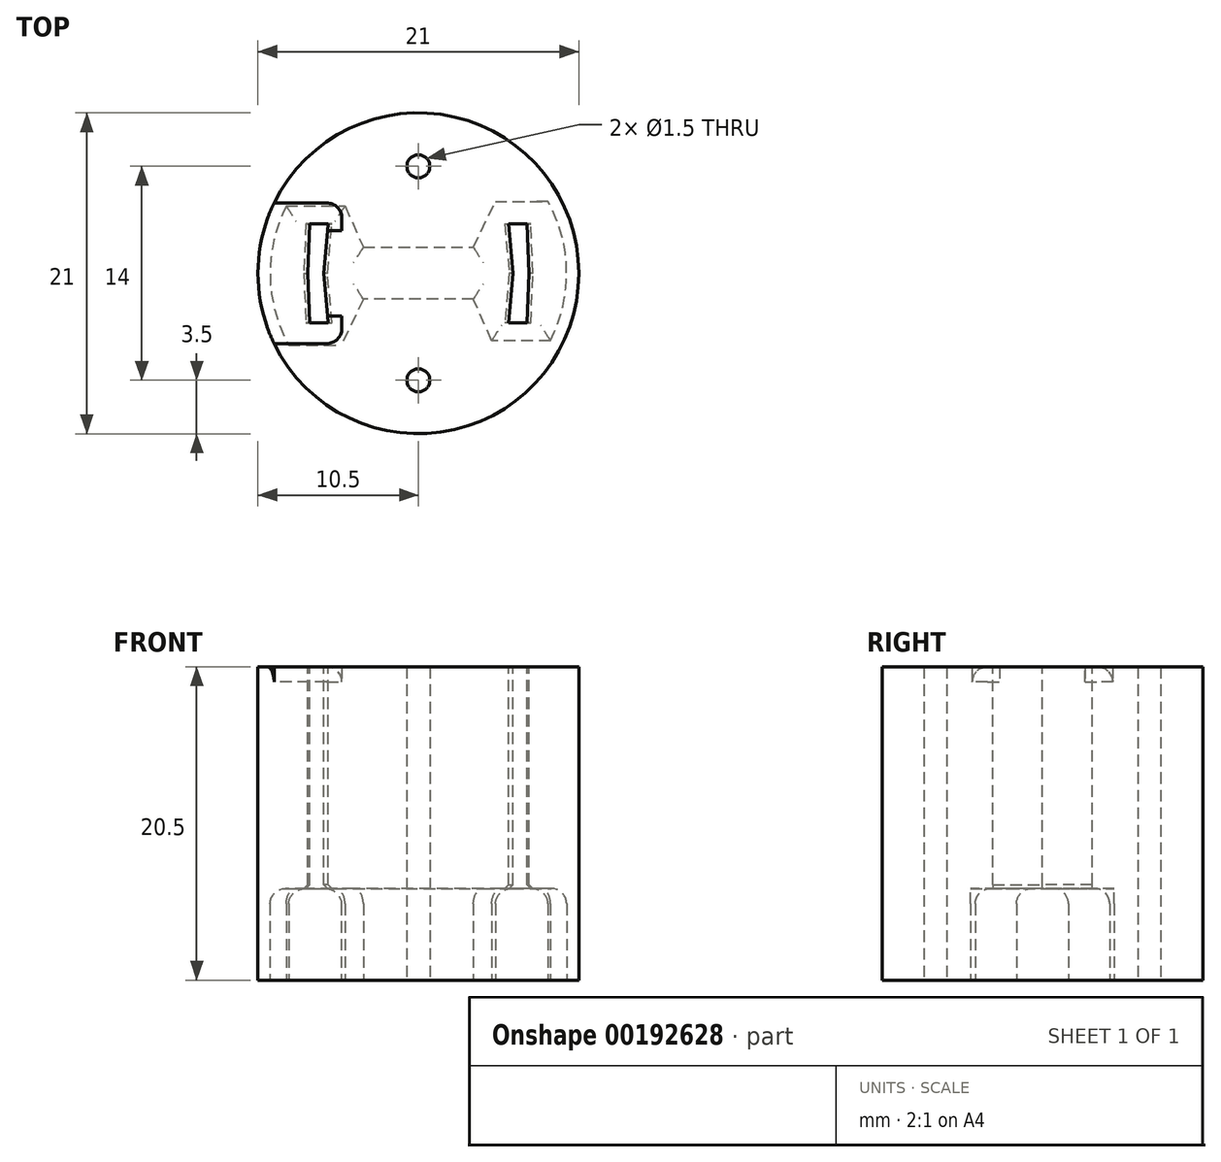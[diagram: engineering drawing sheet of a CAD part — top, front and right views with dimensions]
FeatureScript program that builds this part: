
annotation { "Feature Type Name" : "Feature", "Feature Type Description" : "" }
export const myFeature = defineFeature(function(context is Context, id is Id, definition is map)
    precondition{}
    {
        {
            var Q0;
            Q0=qCreatedBy(makeId("Top.planeOp"),FACE);
            var sketch = newSketch(context, id + "F0", { "sketchPlane" : qUnion([Q0])});
            skCircle(sketch, "E0", {"center": v(0, 0) * mm, "radius": 10.5 * mm});
            skSolve(sketch);
        }
        {
            var Q0;
            Q0=qSketchRegion(id+"F0",true);
            extrude(context, id + "F1", {"entities" : qUnion([Q0]), "oppositeDirection" : true, "depth" : 20.5 * mm});
        }
        {
            var Q0;
            Q0=makeQuery(id+"F1.opExtrude","CAP_FACE",FACE,{"disambiguationData":[OSD([sQuery(id+"F0.wireOp",EDGE,"E0")])],"isStart":false});
            var sketch = newSketch(context, id + "F2", { "sketchPlane" : qUnion([Q0])});
            skArc(sketch, "E1", {"start": v(-6.4, -5.2) * mm, "mid": v(-0.2, -8.25) * mm, "end": v(6.15, -5.5) * mm});
            skLineSegment(sketch, "E2", {"start": v(-8.49, 4.7) * mm, "end": v(-5.04, 4.7) * mm});
            skLineSegment(sketch, "E3", {"start": v(-8.64, -4.4) * mm, "end": v(-4.8, -4.4) * mm});
            skLineSegment(sketch, "E4", {"start": v(8.64, 4.4) * mm, "end": v(4.8, 4.4) * mm});
            skLineSegment(sketch, "E5", {"start": v(4.8, 4.4) * mm, "end": v(3.6, 1.7) * mm});
            skLineSegment(sketch, "E6", {"start": v(3.6, 1.7) * mm, "end": v(-3.6, 1.7) * mm});
            skLineSegment(sketch, "E7", {"start": v(-3.6, 1.7) * mm, "end": v(-5.04, 4.7) * mm});
            skLineSegment(sketch, "E8", {"start": v(-4, 4.4) * mm, "end": v(3.92, 4.4) * mm});
            skLineSegment(sketch, "E9", {"start": v(3.92, 4.4) * mm, "end": v(3.17, 2.7) * mm});
            skLineSegment(sketch, "E10", {"start": v(3.17, 2.7) * mm, "end": v(-3.2, 2.7) * mm});
            skLineSegment(sketch, "E11", {"start": v(-3.2, 2.7) * mm, "end": v(-4, 4.4) * mm});
            skLineSegment(sketch, "E12", {"start": v(-4.8, -4.4) * mm, "end": v(-3.6, -1.7) * mm});
            skLineSegment(sketch, "E13", {"start": v(-3.6, -1.7) * mm, "end": v(3.6, -1.7) * mm});
            skLineSegment(sketch, "E14", {"start": v(4, -4.4) * mm, "end": v(3.2, -2.7) * mm});
            skLineSegment(sketch, "E15", {"start": v(3.2, -2.7) * mm, "end": v(-3.17, -2.7) * mm});
            skLineSegment(sketch, "E16", {"start": v(-3.17, -2.7) * mm, "end": v(-3.92, -4.4) * mm});
            skLineSegment(sketch, "E17", {"start": v(-3.92, -4.4) * mm, "end": v(4, -4.4) * mm});
            skArc(sketch, "E18", {"start": v(-8.64, -4.4) * mm, "mid": v(-9.7, 0.17) * mm, "end": v(-8.49, 4.7) * mm});
            skArc(sketch, "E19", {"start": v(8.64, 4.4) * mm, "mid": v(9.7, -0.17) * mm, "end": v(8.49, -4.7) * mm});
            skLineSegment(sketch, "E20", {"start": v(6.15, -5.5) * mm, "end": v(2.15, -5.5) * mm});
            skLineSegment(sketch, "E21", {"start": v(3.6, -1.7) * mm, "end": v(5.04, -4.7) * mm});
            skLineSegment(sketch, "E22", {"start": v(5.04, -4.7) * mm, "end": v(8.49, -4.7) * mm});
            skLineSegment(sketch, "E23", {"start": v(-2.15, 5.5) * mm, "end": v(-6.15, 5.5) * mm});
            skLineSegment(sketch, "E24.trimOffspring", {"start": v(6.4, 5.2) * mm, "end": v(-2.15, 5.2) * mm});
            skArc(sketch, "E25.trimOffspring", {"start": v(-6.15, 5.5) * mm, "mid": v(0.2, 8.25) * mm, "end": v(6.4, 5.2) * mm});
            skLineSegment(sketch, "E26.trimOffspring", {"start": v(2.15, -5.2) * mm, "end": v(-6.4, -5.2) * mm});
            skLineSegment(sketch, "E27", {"start": v(2.15, -5.2) * mm, "end": v(2.15, -5.5) * mm});
            skLineSegment(sketch, "E28", {"start": v(-2.15, 5.5) * mm, "end": v(-2.15, 5.2) * mm});
            skSolve(sketch);
        }
        {
            var Q0;
            Q0=qSketchRegion(id+"F2",true);
            extrude(context, id + "F3", {"entities" : qUnion([Q0]), "operationType" : NewBodyOperationType.REMOVE, "oppositeDirection" : true, "depth" : 6 * mm});
        }
        {
            var Q0;
            Q0=makeQuery(id+"F1.opExtrude","CAP_FACE",FACE,{"disambiguationData":[OSD([sQuery(id+"F0.wireOp",EDGE,"E0")])],"isStart":false});
            var sketch = newSketch(context, id + "F4", { "sketchPlane" : qUnion([Q0])});
            skCircle(sketch, "E29", {"center": v(0, -7) * mm, "radius": 0.75 * mm});
            skCircle(sketch, "E30", {"center": v(0, 7) * mm, "radius": 0.75 * mm});
            skSolve(sketch);
        }
        {
            var Q0;
            Q0=qSketchRegion(id+"F4",true);
            extrude(context, id + "F5", {"entities" : qUnion([Q0]), "operationType" : NewBodyOperationType.REMOVE, "endBound" : BoundingType.THROUGH_ALL, "oppositeDirection" : true, "depth" : 30 * mm});
        }
        {
            var Q0;
            Q0=makeQuery(id+"F1.opExtrude","CAP_FACE",FACE,{"disambiguationData":[OSD([sQuery(id+"F0.wireOp",EDGE,"E0")])],"isStart":true});
            var sketch = newSketch(context, id + "F6", { "sketchPlane" : qUnion([Q0])});
            skLineSegment(sketch, "E31.bottom", {"start": v(-5, -2.8) * mm, "end": v(-6, -2.8) * mm});
            skLineSegment(sketch, "E31.right", {"start": v(-6, -2.8) * mm, "end": v(-6, 2.8) * mm});
            skArc(sketch, "E32", {"start": v(-9.44, 4.6) * mm, "mid": v(0, 10.5) * mm, "end": v(9.44, 4.6) * mm});
            skArc(sketch, "E33", {"start": v(9.44, -4.6) * mm, "mid": v(0, -10.5) * mm, "end": v(-9.44, -4.6) * mm});
            skLineSegment(sketch, "E34", {"start": v(-9.44, -4.6) * mm, "end": v(-5, -4.6) * mm});
            skLineSegment(sketch, "E35", {"start": v(-5, -4.6) * mm, "end": v(-5, -2.8) * mm});
            skLineSegment(sketch, "E36", {"start": v(-6, 2.8) * mm, "end": v(-5, 2.8) * mm});
            skLineSegment(sketch, "E37", {"start": v(-5, 2.8) * mm, "end": v(-5, 4.6) * mm});
            skLineSegment(sketch, "E38", {"start": v(-5, 4.6) * mm, "end": v(-9.44, 4.6) * mm});
            skLineSegment(sketch, "E39", {"start": v(9.44, 4.6) * mm, "end": v(5, 4.6) * mm});
            skLineSegment(sketch, "E40", {"start": v(5, 2.8) * mm, "end": v(6, 2.8) * mm});
            skLineSegment(sketch, "E41", {"start": v(6, 2.8) * mm, "end": v(6, -2.8) * mm});
            skLineSegment(sketch, "E42", {"start": v(6, -2.8) * mm, "end": v(5, -2.8) * mm});
            skLineSegment(sketch, "E43", {"start": v(5, -2.8) * mm, "end": v(5, -4.6) * mm});
            skLineSegment(sketch, "E44", {"start": v(5, -4.6) * mm, "end": v(9.44, -4.6) * mm});
            skLineSegment(sketch, "E45", {"start": v(5, 4.6) * mm, "end": v(5, 2.8) * mm});
            skSolve(sketch);
        }
        {
            var Q0;
            Q0=qSketchRegion(id+"F6",true);
            extrude(context, id + "F7", {"entities" : qUnion([Q0]), "operationType" : NewBodyOperationType.REMOVE, "oppositeDirection" : true, "depth" : 13 * mm});
        }
        {
            var Q0;
            {var subQ0=sQuery(id+"F0.wireOp",EDGE,"E0");Q0=makeQuery(id+"F7.boolean.opBoolean","SPLIT",FACE,{"disambiguationData":[TD([makeQuery(id+"F7.opExtrude","SWEPT_FACE",FACE,{"disambiguationData":[OSD([sQuery(id+"F6.wireOp",EDGE,"E31.bottom")])]})])],"derivedFrom":makeQuery(id+"F1.opExtrude","CAP_FACE",FACE,{"disambiguationData":[OSD([subQ0])],"isStart":true})});}
            var sketch = newSketch(context, id + "F8", { "sketchPlane" : qUnion([Q0])});
            skLineSegment(sketch, "E46", {"start": v(-5.9, -3.25) * mm, "end": v(-7.1, -3.25) * mm});
            skLineSegment(sketch, "E47", {"start": v(-7.1, -3.25) * mm, "end": v(-7.25, 0) * mm});
            skLineSegment(sketch, "E48", {"start": v(-7.25, 0) * mm, "end": v(-7.1, 3.25) * mm});
            skLineSegment(sketch, "E49", {"start": v(-7.1, 3.25) * mm, "end": v(-5.9, 3.25) * mm});
            skLineSegment(sketch, "E50", {"start": v(5.9, -3.25) * mm, "end": v(7.1, -3.25) * mm});
            skLineSegment(sketch, "E51", {"start": v(7.1, -3.25) * mm, "end": v(7.25, 0) * mm});
            skLineSegment(sketch, "E52", {"start": v(7.25, 0) * mm, "end": v(7.1, 3.25) * mm});
            skLineSegment(sketch, "E53", {"start": v(7.1, 3.25) * mm, "end": v(5.9, 3.25) * mm});
            skLineSegment(sketch, "E54", {"start": v(5.9, -3.25) * mm, "end": v(6.2, 0) * mm});
            skLineSegment(sketch, "E55", {"start": v(6.2, 0) * mm, "end": v(5.9, 3.25) * mm});
            skLineSegment(sketch, "E56", {"start": v(-5.9, 3.25) * mm, "end": v(-6.2, 0) * mm});
            skLineSegment(sketch, "E57", {"start": v(-5.9, -3.25) * mm, "end": v(-6.2, 0) * mm});
            skSolve(sketch);
        }
        {
            var Q0;
            Q0=qSketchRegion(id+"F8",true);
            extrude(context, id + "F9", {"entities" : qUnion([Q0]), "operationType" : NewBodyOperationType.REMOVE, "oppositeDirection" : true, "depth" : 25 * mm});
        }
        {
            var Q0;
            Q0=qCreatedBy(makeId("Right.planeOp"),FACE);
            cPlane(context, id + "F10", {"entities" : qUnion([Q0]), "cplaneType" : CPlaneType.OFFSET, "offset" : 7 * mm, "width" : 150 * mm, "height" : 150 * mm});
        }
        {
            var Q0;
            Q0=qCreatedBy(id+"F10.planeOp",FACE);
            var sketch = newSketch(context, id + "F11", { "sketchPlane" : qUnion([Q0])});
            skLineSegment(sketch, "E58", {"start": v(-2.8, 0) * mm, "end": v(-2.8, -13) * mm});
            skLineSegment(sketch, "E59", {"start": v(-2.8, -13) * mm, "end": v(0, -13) * mm});
            skLineSegment(sketch, "E60", {"start": v(0, -13) * mm, "end": v(2.8, -13) * mm});
            skLineSegment(sketch, "E61", {"start": v(2.8, -13) * mm, "end": v(2.8, 0) * mm});
            skLineSegment(sketch, "E62", {"start": v(2.8, 0) * mm, "end": v(-2.8, 0) * mm});
            skSolve(sketch);
        }
        {
            var Q0;
            Q0=qSketchRegion(id+"F11",true);
            extrude(context, id + "F12", {"entities" : qUnion([Q0]), "operationType" : NewBodyOperationType.REMOVE, "oppositeDirection" : true, "depth" : 14.04 * mm});
        }
        {
            var Q0;
            Q0=makeQuery(id+"F3.boolean.opBoolean","COPY",EDGE,{"derivedFrom":makeQuery(id+"F3.opExtrude","CAP_EDGE",EDGE,{"disambiguationData":[OSD([sQuery(id+"F2.wireOp",EDGE,"E6")])],"isStart":false})});
            var Q1;
            Q1=makeQuery(id+"F3.boolean.opBoolean","COPY",EDGE,{"derivedFrom":makeQuery(id+"F3.opExtrude","CAP_EDGE",EDGE,{"disambiguationData":[OSD([sQuery(id+"F2.wireOp",EDGE,"E13")])],"isStart":false})});
            var Q2;
            Q2=makeQuery(id+"F3.boolean.opBoolean","COPY",EDGE,{"derivedFrom":makeQuery(id+"F3.opExtrude","CAP_EDGE",EDGE,{"disambiguationData":[OSD([sQuery(id+"F2.wireOp",EDGE,"E21")])],"isStart":false})});
            var Q3;
            Q3=makeQuery(id+"F3.boolean.opBoolean","COPY",EDGE,{"derivedFrom":makeQuery(id+"F3.opExtrude","CAP_EDGE",EDGE,{"disambiguationData":[OSD([sQuery(id+"F2.wireOp",EDGE,"E7")])],"isStart":false})});
            var Q4;
            Q4=makeQuery(id+"F3.boolean.opBoolean","COPY",EDGE,{"derivedFrom":makeQuery(id+"F3.opExtrude","CAP_EDGE",EDGE,{"disambiguationData":[OSD([sQuery(id+"F2.wireOp",EDGE,"E19")])],"isStart":false})});
            var Q5;
            Q5=makeQuery(id+"F3.boolean.opBoolean","COPY",EDGE,{"derivedFrom":makeQuery(id+"F3.opExtrude","CAP_EDGE",EDGE,{"disambiguationData":[OSD([sQuery(id+"F2.wireOp",EDGE,"E4")])],"isStart":false})});
            var Q6;
            Q6=makeQuery(id+"F3.boolean.opBoolean","COPY",EDGE,{"derivedFrom":makeQuery(id+"F3.opExtrude","CAP_EDGE",EDGE,{"disambiguationData":[OSD([sQuery(id+"F2.wireOp",EDGE,"E18")])],"isStart":false})});
            var Q7;
            Q7=makeQuery(id+"F3.boolean.opBoolean","COPY",EDGE,{"derivedFrom":makeQuery(id+"F3.opExtrude","CAP_EDGE",EDGE,{"disambiguationData":[OSD([sQuery(id+"F2.wireOp",EDGE,"E3")])],"isStart":false})});
            var Q8;
            Q8=makeQuery(id+"F3.boolean.opBoolean","COPY",EDGE,{"derivedFrom":makeQuery(id+"F3.opExtrude","CAP_EDGE",EDGE,{"disambiguationData":[OSD([sQuery(id+"F2.wireOp",EDGE,"E12")])],"isStart":false})});
            var Q9;
            Q9=makeQuery(id+"F3.boolean.opBoolean","COPY",EDGE,{"derivedFrom":makeQuery(id+"F3.opExtrude","CAP_EDGE",EDGE,{"disambiguationData":[OSD([sQuery(id+"F2.wireOp",EDGE,"E5")])],"isStart":false})});
            fillet(context, id + "F13", {"entities" : qUnion([Q0, Q1, Q2, Q3, Q4, Q5, Q6, Q7, Q8, Q9]), "radius" : 1 * mm, "tangentPropagation" : true, "allowEdgeOverflow" : false});
        }
        {
            var Q0;
            Q0=makeQuery(id+"F9.boolean.opBoolean","INTERSECT",EDGE,{"derivedFrom":[makeQuery(id+"F3.boolean.opBoolean","COPY",FACE,{"derivedFrom":makeQuery(id+"F3.opExtrude","CAP_FACE",FACE,{"disambiguationData":[OSD([sQuery(id+"F2.wireOp",EDGE,"E2"),sQuery(id+"F2.wireOp",EDGE,"E3"),sQuery(id+"F2.wireOp",EDGE,"E4"),sQuery(id+"F2.wireOp",EDGE,"E5"),sQuery(id+"F2.wireOp",EDGE,"E6"),sQuery(id+"F2.wireOp",EDGE,"E7"),sQuery(id+"F2.wireOp",EDGE,"E12"),sQuery(id+"F2.wireOp",EDGE,"E13"),sQuery(id+"F2.wireOp",EDGE,"E18"),sQuery(id+"F2.wireOp",EDGE,"E19"),sQuery(id+"F2.wireOp",EDGE,"E21"),sQuery(id+"F2.wireOp",EDGE,"E22")])],"isStart":false})}),makeQuery(id+"F9.opExtrude","SWEPT_FACE",FACE,{"disambiguationData":[OSD([sQuery(id+"F8.wireOp",EDGE,"E51")])]})]});
            var Q1;
            Q1=makeQuery(id+"F9.boolean.opBoolean","INTERSECT",EDGE,{"derivedFrom":[makeQuery(id+"F3.boolean.opBoolean","COPY",FACE,{"derivedFrom":makeQuery(id+"F3.opExtrude","CAP_FACE",FACE,{"disambiguationData":[OSD([sQuery(id+"F2.wireOp",EDGE,"E2"),sQuery(id+"F2.wireOp",EDGE,"E3"),sQuery(id+"F2.wireOp",EDGE,"E4"),sQuery(id+"F2.wireOp",EDGE,"E5"),sQuery(id+"F2.wireOp",EDGE,"E6"),sQuery(id+"F2.wireOp",EDGE,"E7"),sQuery(id+"F2.wireOp",EDGE,"E12"),sQuery(id+"F2.wireOp",EDGE,"E13"),sQuery(id+"F2.wireOp",EDGE,"E18"),sQuery(id+"F2.wireOp",EDGE,"E19"),sQuery(id+"F2.wireOp",EDGE,"E21"),sQuery(id+"F2.wireOp",EDGE,"E22")])],"isStart":false})}),makeQuery(id+"F9.opExtrude","SWEPT_FACE",FACE,{"disambiguationData":[OSD([sQuery(id+"F8.wireOp",EDGE,"E52")])]})]});
            var Q2;
            Q2=makeQuery(id+"F9.boolean.opBoolean","INTERSECT",EDGE,{"derivedFrom":[makeQuery(id+"F3.boolean.opBoolean","COPY",FACE,{"derivedFrom":makeQuery(id+"F3.opExtrude","CAP_FACE",FACE,{"disambiguationData":[OSD([sQuery(id+"F2.wireOp",EDGE,"E2"),sQuery(id+"F2.wireOp",EDGE,"E3"),sQuery(id+"F2.wireOp",EDGE,"E4"),sQuery(id+"F2.wireOp",EDGE,"E5"),sQuery(id+"F2.wireOp",EDGE,"E6"),sQuery(id+"F2.wireOp",EDGE,"E7"),sQuery(id+"F2.wireOp",EDGE,"E12"),sQuery(id+"F2.wireOp",EDGE,"E13"),sQuery(id+"F2.wireOp",EDGE,"E18"),sQuery(id+"F2.wireOp",EDGE,"E19"),sQuery(id+"F2.wireOp",EDGE,"E21"),sQuery(id+"F2.wireOp",EDGE,"E22")])],"isStart":false})}),makeQuery(id+"F9.opExtrude","SWEPT_FACE",FACE,{"disambiguationData":[OSD([sQuery(id+"F8.wireOp",EDGE,"E47")])]})]});
            var Q3;
            Q3=makeQuery(id+"F9.boolean.opBoolean","INTERSECT",EDGE,{"derivedFrom":[makeQuery(id+"F3.boolean.opBoolean","COPY",FACE,{"derivedFrom":makeQuery(id+"F3.opExtrude","CAP_FACE",FACE,{"disambiguationData":[OSD([sQuery(id+"F2.wireOp",EDGE,"E2"),sQuery(id+"F2.wireOp",EDGE,"E3"),sQuery(id+"F2.wireOp",EDGE,"E4"),sQuery(id+"F2.wireOp",EDGE,"E5"),sQuery(id+"F2.wireOp",EDGE,"E6"),sQuery(id+"F2.wireOp",EDGE,"E7"),sQuery(id+"F2.wireOp",EDGE,"E12"),sQuery(id+"F2.wireOp",EDGE,"E13"),sQuery(id+"F2.wireOp",EDGE,"E18"),sQuery(id+"F2.wireOp",EDGE,"E19"),sQuery(id+"F2.wireOp",EDGE,"E21"),sQuery(id+"F2.wireOp",EDGE,"E22")])],"isStart":false})}),makeQuery(id+"F9.opExtrude","SWEPT_FACE",FACE,{"disambiguationData":[OSD([sQuery(id+"F8.wireOp",EDGE,"E48")])]})]});
            var Q4;
            Q4=makeQuery(id+"F9.boolean.opBoolean","INTERSECT",EDGE,{"derivedFrom":[makeQuery(id+"F3.boolean.opBoolean","COPY",FACE,{"derivedFrom":makeQuery(id+"F3.opExtrude","CAP_FACE",FACE,{"disambiguationData":[OSD([sQuery(id+"F2.wireOp",EDGE,"E2"),sQuery(id+"F2.wireOp",EDGE,"E3"),sQuery(id+"F2.wireOp",EDGE,"E4"),sQuery(id+"F2.wireOp",EDGE,"E5"),sQuery(id+"F2.wireOp",EDGE,"E6"),sQuery(id+"F2.wireOp",EDGE,"E7"),sQuery(id+"F2.wireOp",EDGE,"E12"),sQuery(id+"F2.wireOp",EDGE,"E13"),sQuery(id+"F2.wireOp",EDGE,"E18"),sQuery(id+"F2.wireOp",EDGE,"E19"),sQuery(id+"F2.wireOp",EDGE,"E21"),sQuery(id+"F2.wireOp",EDGE,"E22")])],"isStart":false})}),makeQuery(id+"F9.opExtrude","SWEPT_FACE",FACE,{"disambiguationData":[OSD([sQuery(id+"F8.wireOp",EDGE,"E54")])]})]});
            var Q5;
            Q5=makeQuery(id+"F9.boolean.opBoolean","INTERSECT",EDGE,{"derivedFrom":[makeQuery(id+"F3.boolean.opBoolean","COPY",FACE,{"derivedFrom":makeQuery(id+"F3.opExtrude","CAP_FACE",FACE,{"disambiguationData":[OSD([sQuery(id+"F2.wireOp",EDGE,"E2"),sQuery(id+"F2.wireOp",EDGE,"E3"),sQuery(id+"F2.wireOp",EDGE,"E4"),sQuery(id+"F2.wireOp",EDGE,"E5"),sQuery(id+"F2.wireOp",EDGE,"E6"),sQuery(id+"F2.wireOp",EDGE,"E7"),sQuery(id+"F2.wireOp",EDGE,"E12"),sQuery(id+"F2.wireOp",EDGE,"E13"),sQuery(id+"F2.wireOp",EDGE,"E18"),sQuery(id+"F2.wireOp",EDGE,"E19"),sQuery(id+"F2.wireOp",EDGE,"E21"),sQuery(id+"F2.wireOp",EDGE,"E22")])],"isStart":false})}),makeQuery(id+"F9.opExtrude","SWEPT_FACE",FACE,{"disambiguationData":[OSD([sQuery(id+"F8.wireOp",EDGE,"E55")])]})]});
            var Q6;
            Q6=makeQuery(id+"F9.boolean.opBoolean","INTERSECT",EDGE,{"derivedFrom":[makeQuery(id+"F3.boolean.opBoolean","COPY",FACE,{"derivedFrom":makeQuery(id+"F3.opExtrude","CAP_FACE",FACE,{"disambiguationData":[OSD([sQuery(id+"F2.wireOp",EDGE,"E2"),sQuery(id+"F2.wireOp",EDGE,"E3"),sQuery(id+"F2.wireOp",EDGE,"E4"),sQuery(id+"F2.wireOp",EDGE,"E5"),sQuery(id+"F2.wireOp",EDGE,"E6"),sQuery(id+"F2.wireOp",EDGE,"E7"),sQuery(id+"F2.wireOp",EDGE,"E12"),sQuery(id+"F2.wireOp",EDGE,"E13"),sQuery(id+"F2.wireOp",EDGE,"E18"),sQuery(id+"F2.wireOp",EDGE,"E19"),sQuery(id+"F2.wireOp",EDGE,"E21"),sQuery(id+"F2.wireOp",EDGE,"E22")])],"isStart":false})}),makeQuery(id+"F9.opExtrude","SWEPT_FACE",FACE,{"disambiguationData":[OSD([sQuery(id+"F8.wireOp",EDGE,"E57")])]})]});
            var Q7;
            Q7=makeQuery(id+"F9.boolean.opBoolean","INTERSECT",EDGE,{"derivedFrom":[makeQuery(id+"F3.boolean.opBoolean","COPY",FACE,{"derivedFrom":makeQuery(id+"F3.opExtrude","CAP_FACE",FACE,{"disambiguationData":[OSD([sQuery(id+"F2.wireOp",EDGE,"E2"),sQuery(id+"F2.wireOp",EDGE,"E3"),sQuery(id+"F2.wireOp",EDGE,"E4"),sQuery(id+"F2.wireOp",EDGE,"E5"),sQuery(id+"F2.wireOp",EDGE,"E6"),sQuery(id+"F2.wireOp",EDGE,"E7"),sQuery(id+"F2.wireOp",EDGE,"E12"),sQuery(id+"F2.wireOp",EDGE,"E13"),sQuery(id+"F2.wireOp",EDGE,"E18"),sQuery(id+"F2.wireOp",EDGE,"E19"),sQuery(id+"F2.wireOp",EDGE,"E21"),sQuery(id+"F2.wireOp",EDGE,"E22")])],"isStart":false})}),makeQuery(id+"F9.opExtrude","SWEPT_FACE",FACE,{"disambiguationData":[OSD([sQuery(id+"F8.wireOp",EDGE,"E56")])]})]});
            chamfer(context, id + "F14", {"entities" : qUnion([Q0, Q1, Q2, Q3, Q4, Q5, Q6, Q7]), "width" : .25 * mm, "tangentPropagation" : true});
        }
        {
            var Q0;
            Q0=makeQuery(id+"F2.imprint","IMPRINT",FACE,{"disambiguationData":[TD([[makeQuery(id+"F2.imprint","IMPRINT",EDGE,{"derivedFrom":sQuery(id+"F2.wireOp",EDGE,"E23")}),-1.0]])]});
            var sketch = newSketch(context, id + "F15", { "sketchPlane" : qUnion([Q0])});
            skLineSegment(sketch, "E63.0", {"start": v(0.7, 6.76) * mm, "end": v(0.7, 6.76) * mm});
            skLineSegment(sketch, "E64.0.0", {"start": v(-6.15, 5.5) * mm, "end": v(-2.15, 5.5) * mm});
            skLineSegment(sketch, "E64.0.1", {"start": v(-2.15, 5.5) * mm, "end": v(-2.15, 5.2) * mm});
            skLineSegment(sketch, "E64.0.2", {"start": v(-2.15, 5.2) * mm, "end": v(6.4, 5.2) * mm});
            skArc(sketch, "E64.0.3", {"start": v(6.4, 5.2) * mm, "mid": v(0.2, 8.25) * mm, "end": v(-6.15, 5.5) * mm});
            skLineSegment(sketch, "E65.0", {"start": v(-0.7, -6.72) * mm, "end": v(-0.7, -6.72) * mm});
            skLineSegment(sketch, "E66.0.0", {"start": v(2.15, -5.2) * mm, "end": v(-6.4, -5.2) * mm});
            skArc(sketch, "E66.0.1", {"start": v(-6.4, -5.2) * mm, "mid": v(-0.2, -8.25) * mm, "end": v(6.15, -5.5) * mm});
            skLineSegment(sketch, "E66.0.2", {"start": v(6.15, -5.5) * mm, "end": v(2.15, -5.5) * mm});
            skLineSegment(sketch, "E66.0.3", {"start": v(2.15, -5.5) * mm, "end": v(2.15, -5.2) * mm});
            skCircle(sketch, "E67.0", {"center": v(0, 7) * mm, "radius": 0.75 * mm});
            skCircle(sketch, "E68.0", {"center": v(0, -7) * mm, "radius": 0.75 * mm});
            skSolve(sketch);
        }
        {
            var Q0;
            Q0=makeQuery(id+"F2.imprint","IMPRINT",FACE,{"disambiguationData":[TD([[makeQuery(id+"F2.imprint","IMPRINT",EDGE,{"derivedFrom":sQuery(id+"F2.wireOp",EDGE,"E1")}),-1.0]])]});
            var sketch = newSketch(context, id + "F16", { "sketchPlane" : qUnion([Q0])});
            skLineSegment(sketch, "E69.0.0", {"start": v(2.15, -5.2) * mm, "end": v(-6.4, -5.2) * mm});
            skArc(sketch, "E69.0.1", {"start": v(-6.4, -5.2) * mm, "mid": v(-0.2, -8.25) * mm, "end": v(6.15, -5.5) * mm});
            skLineSegment(sketch, "E69.0.2", {"start": v(6.15, -5.5) * mm, "end": v(2.15, -5.5) * mm});
            skLineSegment(sketch, "E69.0.3", {"start": v(2.15, -5.5) * mm, "end": v(2.15, -5.2) * mm});
            skLineSegment(sketch, "E70.0.0", {"start": v(-3.92, -4.4) * mm, "end": v(4, -4.4) * mm});
            skLineSegment(sketch, "E70.0.1", {"start": v(4, -4.4) * mm, "end": v(3.2, -2.7) * mm});
            skLineSegment(sketch, "E70.0.2", {"start": v(3.2, -2.7) * mm, "end": v(-3.17, -2.7) * mm});
            skLineSegment(sketch, "E70.0.3", {"start": v(-3.17, -2.7) * mm, "end": v(-3.92, -4.4) * mm});
            skLineSegment(sketch, "E71.0.0", {"start": v(3.92, 4.4) * mm, "end": v(-4, 4.4) * mm});
            skLineSegment(sketch, "E71.0.1", {"start": v(-4, 4.4) * mm, "end": v(-3.2, 2.7) * mm});
            skLineSegment(sketch, "E71.0.2", {"start": v(-3.2, 2.7) * mm, "end": v(3.17, 2.7) * mm});
            skLineSegment(sketch, "E71.0.3", {"start": v(3.17, 2.7) * mm, "end": v(3.92, 4.4) * mm});
            skLineSegment(sketch, "E72.0.0", {"start": v(-6.15, 5.5) * mm, "end": v(-2.15, 5.5) * mm});
            skLineSegment(sketch, "E72.0.1", {"start": v(-2.15, 5.5) * mm, "end": v(-2.15, 5.2) * mm});
            skLineSegment(sketch, "E72.0.2", {"start": v(-2.15, 5.2) * mm, "end": v(6.4, 5.2) * mm});
            skArc(sketch, "E72.0.3", {"start": v(6.4, 5.2) * mm, "mid": v(0.2, 8.25) * mm, "end": v(-6.15, 5.5) * mm});
            skSolve(sketch);
        }
        {
            var Q0;
            Q0 = qSketchRegion(id + "F16", true);
            extrude(context, id + "F17", {"entities" : qUnion([Q0]), "operationType" : NewBodyOperationType.ADD, "oppositeDirection" : true, "depth" : 6 * mm});
        }
        {
            var Q0;
            Q0=makeQuery(id+"F2.imprint","IMPRINT",FACE,{"disambiguationData":[TD([[makeQuery(id+"F2.imprint","IMPRINT",EDGE,{"derivedFrom":sQuery(id+"F2.wireOp",EDGE,"E1")}),-1.0]])]});
            var sketch = newSketch(context, id + "F18", { "sketchPlane" : qUnion([Q0])});
            skCircle(sketch, "E73.0", {"center": v(0, 7) * mm, "radius": 0.75 * mm});
            skCircle(sketch, "E74.0", {"center": v(0, -7) * mm, "radius": 0.75 * mm});
            skSolve(sketch);
        }
        {
            var Q0;
            Q0 = qSketchRegion(id + "F18", true);
            extrude(context, id + "F19", {"entities" : qUnion([Q0]), "operationType" : NewBodyOperationType.REMOVE, "oppositeDirection" : true, "depth" : 25 * mm});
        }
        {
            var Q0;
            Q0=makeQuery(id+"F7.boolean.opBoolean","COPY",EDGE,{"derivedFrom":makeQuery(id+"F7.opExtrude","CAP_EDGE",EDGE,{"disambiguationData":[OSD([sQuery(id+"F6.wireOp",EDGE,"E34")])],"isStart":true})});
            var Q1;
            Q1=makeQuery(id+"F7.boolean.opBoolean","COPY",EDGE,{"derivedFrom":makeQuery(id+"F7.opExtrude","CAP_EDGE",EDGE,{"disambiguationData":[OSD([sQuery(id+"F6.wireOp",EDGE,"E35")])],"isStart":true})});
            var Q2;
            Q2=makeQuery(id+"F7.boolean.opBoolean","COPY",EDGE,{"derivedFrom":makeQuery(id+"F7.opExtrude","CAP_EDGE",EDGE,{"disambiguationData":[OSD([sQuery(id+"F6.wireOp",EDGE,"E37")])],"isStart":true})});
            var Q3;
            Q3=makeQuery(id+"F7.boolean.opBoolean","COPY",EDGE,{"derivedFrom":makeQuery(id+"F7.opExtrude","CAP_EDGE",EDGE,{"disambiguationData":[OSD([sQuery(id+"F6.wireOp",EDGE,"E38")])],"isStart":true})});
            var Q4;
            Q4=makeQuery(id+"F7.boolean.opBoolean","COPY",EDGE,{"derivedFrom":makeQuery(id+"F7.opExtrude","CAP_EDGE",EDGE,{"disambiguationData":[OSD([sQuery(id+"F6.wireOp",EDGE,"E44")])],"isStart":true})});
            var Q5;
            Q5=makeQuery(id+"F7.boolean.opBoolean","COPY",EDGE,{"derivedFrom":makeQuery(id+"F7.opExtrude","CAP_EDGE",EDGE,{"disambiguationData":[OSD([sQuery(id+"F6.wireOp",EDGE,"E43")])],"isStart":true})});
            var Q6;
            Q6=makeQuery(id+"F7.boolean.opBoolean","COPY",EDGE,{"derivedFrom":makeQuery(id+"F7.opExtrude","CAP_EDGE",EDGE,{"disambiguationData":[OSD([sQuery(id+"F6.wireOp",EDGE,"E45")])],"isStart":true})});
            var Q7;
            Q7=makeQuery(id+"F7.boolean.opBoolean","COPY",EDGE,{"derivedFrom":makeQuery(id+"F7.opExtrude","CAP_EDGE",EDGE,{"disambiguationData":[OSD([sQuery(id+"F6.wireOp",EDGE,"E39")])],"isStart":true})});
            fillet(context, id + "F20", {"entities" : qUnion([Q0, Q1, Q2, Q3, Q4, Q5, Q6, Q7]), "radius" : 1 * mm, "tangentPropagation" : true, "allowEdgeOverflow" : false});
        }
        {
            var Q0;
            Q0=makeQuery(id+"F20.opFillet","BLEND_EDGE",EDGE,{"blendedFrom":[makeQuery(id+"F7.boolean.opBoolean","COPY",EDGE,{"derivedFrom":makeQuery(id+"F7.opExtrude","CAP_EDGE",EDGE,{"disambiguationData":[OSD([sQuery(id+"F6.wireOp",EDGE,"E34")])],"isStart":true})}),makeQuery(id+"F7.boolean.opBoolean","COPY",EDGE,{"derivedFrom":makeQuery(id+"F7.opExtrude","CAP_EDGE",EDGE,{"disambiguationData":[OSD([sQuery(id+"F6.wireOp",EDGE,"E35")])],"isStart":true})})],"blendedInto":[]});
            var Q1;
            Q1=makeQuery(id+"F20.opFillet","BLEND_EDGE",EDGE,{"blendedFrom":[makeQuery(id+"F7.boolean.opBoolean","COPY",EDGE,{"derivedFrom":makeQuery(id+"F7.opExtrude","CAP_EDGE",EDGE,{"disambiguationData":[OSD([sQuery(id+"F6.wireOp",EDGE,"E43")])],"isStart":true})}),makeQuery(id+"F7.boolean.opBoolean","COPY",EDGE,{"derivedFrom":makeQuery(id+"F7.opExtrude","CAP_EDGE",EDGE,{"disambiguationData":[OSD([sQuery(id+"F6.wireOp",EDGE,"E44")])],"isStart":true})})],"blendedInto":[]});
            var Q2;
            Q2=makeQuery(id+"F20.opFillet","BLEND_EDGE",EDGE,{"blendedFrom":[makeQuery(id+"F7.boolean.opBoolean","COPY",EDGE,{"derivedFrom":makeQuery(id+"F7.opExtrude","CAP_EDGE",EDGE,{"disambiguationData":[OSD([sQuery(id+"F6.wireOp",EDGE,"E37")])],"isStart":true})}),makeQuery(id+"F7.boolean.opBoolean","COPY",EDGE,{"derivedFrom":makeQuery(id+"F7.opExtrude","CAP_EDGE",EDGE,{"disambiguationData":[OSD([sQuery(id+"F6.wireOp",EDGE,"E38")])],"isStart":true})})],"blendedInto":[]});
            var Q3;
            Q3=makeQuery(id+"F20.opFillet","BLEND_EDGE",EDGE,{"blendedFrom":[makeQuery(id+"F7.boolean.opBoolean","COPY",EDGE,{"derivedFrom":makeQuery(id+"F7.opExtrude","CAP_EDGE",EDGE,{"disambiguationData":[OSD([sQuery(id+"F6.wireOp",EDGE,"E39")])],"isStart":true})}),makeQuery(id+"F7.boolean.opBoolean","COPY",EDGE,{"derivedFrom":makeQuery(id+"F7.opExtrude","CAP_EDGE",EDGE,{"disambiguationData":[OSD([sQuery(id+"F6.wireOp",EDGE,"E45")])],"isStart":true})})],"blendedInto":[]});
            fillet(context, id + "F21", {"entities" : qUnion([Q0, Q1, Q2, Q3]), "radius" : 1 * mm, "tangentPropagation" : true, "allowEdgeOverflow" : false});
        }
        {
            var Q0;
            Q0=makeQuery(id+"F12.boolean.opBoolean","MERGE",FACE,{"derivedFrom":[makeQuery(id+"F7.boolean.opBoolean","COPY",FACE,{"derivedFrom":makeQuery(id+"F7.opExtrude","CAP_FACE",FACE,{"disambiguationData":[OSD([sQuery(id+"F6.wireOp",EDGE,"E31.bottom"),sQuery(id+"F6.wireOp",EDGE,"E31.right"),sQuery(id+"F6.wireOp",EDGE,"E32"),sQuery(id+"F6.wireOp",EDGE,"E33"),sQuery(id+"F6.wireOp",EDGE,"E34"),sQuery(id+"F6.wireOp",EDGE,"E35"),sQuery(id+"F6.wireOp",EDGE,"E36"),sQuery(id+"F6.wireOp",EDGE,"E37"),sQuery(id+"F6.wireOp",EDGE,"E38"),sQuery(id+"F6.wireOp",EDGE,"E39"),sQuery(id+"F6.wireOp",EDGE,"E40"),sQuery(id+"F6.wireOp",EDGE,"E41"),sQuery(id+"F6.wireOp",EDGE,"E42"),sQuery(id+"F6.wireOp",EDGE,"E43"),sQuery(id+"F6.wireOp",EDGE,"E44"),sQuery(id+"F6.wireOp",EDGE,"E45")])],"isStart":false})}),makeQuery(id+"F12.opExtrude","SWEPT_FACE",FACE,{"disambiguationData":[OSD([sQuery(id+"F11.wireOp",EDGE,"E59"),sQuery(id+"F11.wireOp",EDGE,"E60")])]})]});
            extrude(context, id + "F22", {"entities" : qUnion([Q0]), "operationType" : NewBodyOperationType.ADD, "depth" : 13 * mm});
        }
    });
